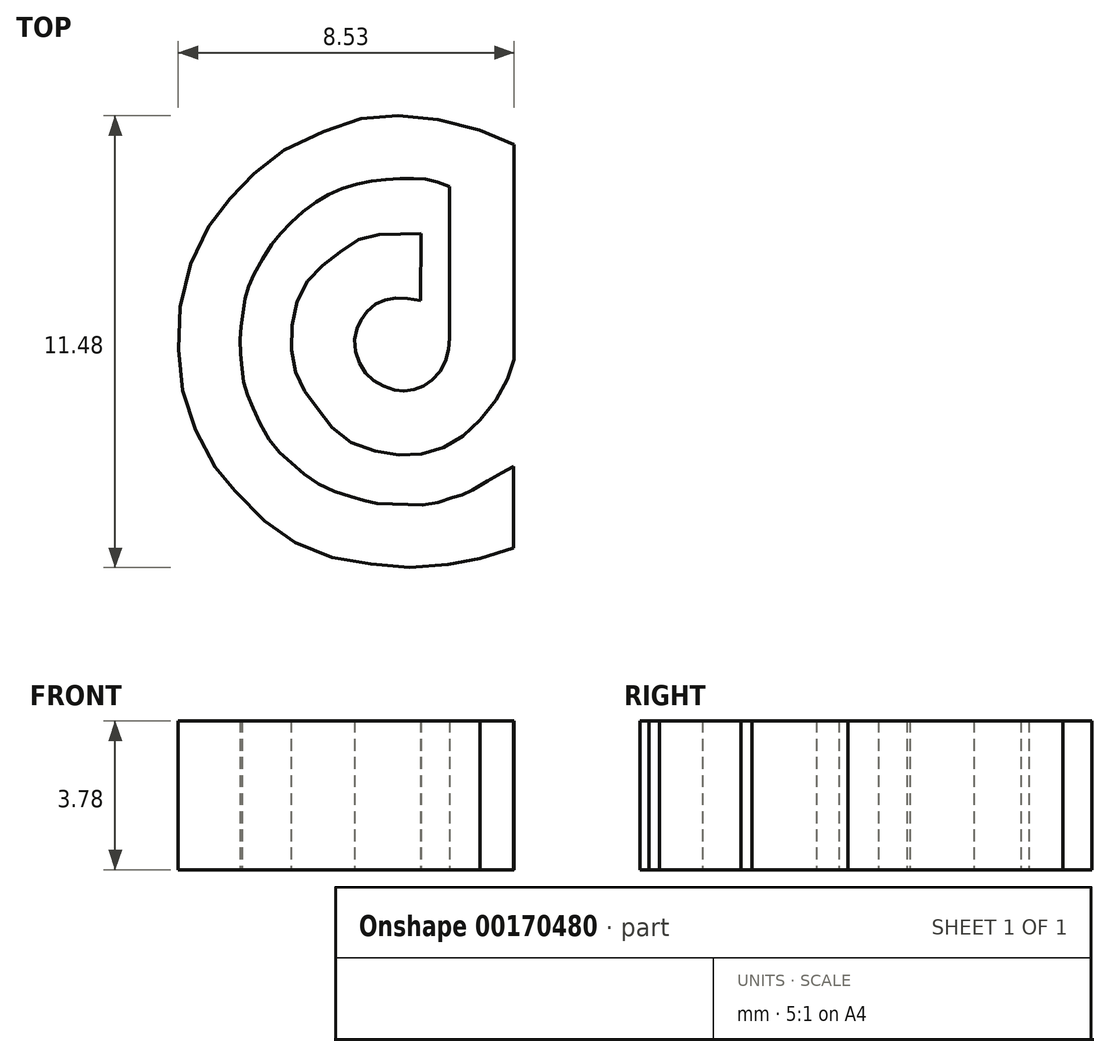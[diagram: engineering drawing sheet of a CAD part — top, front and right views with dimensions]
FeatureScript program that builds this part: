
annotation { "Feature Type Name" : "Feature", "Feature Type Description" : "" }
export const myFeature = defineFeature(function(context is Context, id is Id, definition is map)
    precondition{}
    {
        {
            var Q0;
            Q0=qCreatedBy(makeId("Top.planeOp"),FACE);
            var sketch = newSketch(context, id + "F0", { "sketchPlane" : qUnion([Q0])});
            skFitSpline(sketch, "E0", {"points": [v(23.4, 26.63) * mm, v(22.67, 26.61) * mm, v(21.9, 26.5) * mm, v(21.2, 26.04) * mm, v(20.6, 25.52) * mm, v(20.2, 24.71) * mm, v(20.11, 23.68) * mm, v(20.3, 22.87) * mm, v(20.76, 22.21) * mm, v(21.37, 21.48) * mm, v(22.37, 21.08) * mm, v(23.3, 21) * mm, v(24.15, 21.27) * mm, v(24.85, 21.82) * mm, v(25.5, 22.7) * mm, v(25.77, 23.43) * mm], "startDerivative": vector(-11.94, -0.24) * mm, "endDerivative": vector(3.35, 11.29) * mm});
            skLineSegment(sketch, "E1", {"start": v(25.77, 23.43) * mm, "end": v(25.77, 28.89) * mm});
            skFitSpline(sketch, "E2", {"points": [v(25.77, 28.89) * mm, v(24.88, 29.26) * mm, v(23.67, 29.54) * mm, v(22.63, 29.62) * mm, v(21.68, 29.5) * mm, v(20.6, 29.08) * mm, v(19.53, 28.5) * mm, v(18.93, 27.88) * mm, v(18.33, 27.28) * mm, v(17.85, 26.52) * mm, v(17.37, 25.3) * mm, v(17.24, 24.04) * mm, v(17.31, 22.84) * mm, v(17.63, 21.75) * mm, v(18.18, 20.67) * mm, v(18.57, 20.2) * mm, v(19.4, 19.36) * mm, v(20.16, 18.8) * mm, v(21.17, 18.38) * mm, v(22.2, 18.22) * mm, v(23.22, 18.14) * mm, v(24.21, 18.23) * mm, v(24.9, 18.37) * mm], "startDerivative": vector(-19.04, 9.03) * mm, "endDerivative": vector(17.46, 3.76) * mm});
            skLineSegment(sketch, "E3", {"start": v(25.75, 20.7) * mm, "end": v(25.75, 18.64) * mm});
            skFitSpline(sketch, "E4", {"points": [v(24.9, 18.37) * mm, v(25.75, 18.64) * mm], "startDerivative": vector(0.85, 0.27) * mm, "endDerivative": vector(0.85, 0.27) * mm});
            skFitSpline(sketch, "E5", {"points": [v(25.75, 20.7) * mm, v(25.2, 20.4) * mm, v(24.53, 20.01) * mm, v(24.32, 19.95) * mm, v(23.66, 19.74) * mm, v(23.01, 19.74) * mm, v(22.28, 19.77) * mm, v(21.76, 19.9) * mm, v(20.95, 20.18) * mm, v(20.22, 20.7) * mm, v(19.66, 21.24) * mm, v(19.18, 22.08) * mm, v(18.96, 22.65) * mm, v(18.86, 23.2) * mm], "startDerivative": vector(-6.86, -3.5) * mm, "endDerivative": vector(-0.17, 7.63) * mm});
            skFitSpline(sketch, "E6", {"points": [v(18.86, 23.2) * mm, v(18.8, 23.86) * mm, v(18.86, 24.43) * mm, v(18.96, 25.04) * mm, v(19.14, 25.54) * mm, v(19.59, 26.3) * mm, v(20.01, 26.82) * mm, v(20.65, 27.37) * mm, v(21.23, 27.7) * mm, v(21.95, 27.93) * mm, v(22.6, 28) * mm, v(23.19, 28.02) * mm, v(23.65, 27.99) * mm, v(24.13, 27.82) * mm], "startDerivative": vector(-0.92, 8.73) * mm, "endDerivative": vector(7.09, -2.85) * mm});
            skLineSegment(sketch, "E7", {"start": v(24.13, 27.82) * mm, "end": v(24.13, 24.2) * mm});
            skFitSpline(sketch, "E8", {"points": [v(24.13, 24.2) * mm, v(24.13, 23.93) * mm, v(24.07, 23.5) * mm, v(23.88, 23.12) * mm, v(23.6, 22.83) * mm, v(23.32, 22.7) * mm, v(22.99, 22.62) * mm, v(22.7, 22.66) * mm, v(22.3, 22.82) * mm, v(22, 23.07) * mm, v(21.8, 23.46) * mm, v(21.71, 23.89) * mm, v(21.8, 24.27) * mm, v(21.93, 24.51) * mm, v(22.2, 24.8) * mm, v(22.52, 24.95) * mm, v(22.88, 25) * mm, v(23.39, 24.92) * mm], "startDerivative": vector(0.09, -4.95) * mm, "endDerivative": vector(7.74, -1.48) * mm});
            skLineSegment(sketch, "E9", {"start": v(23.4, 26.63) * mm, "end": v(23.39, 24.92) * mm});
            skSolve(sketch);
        }
        {
            var Q0;
            Q0=makeQuery(id+"F0.imprint","IMPRINT",FACE,{"disambiguationData":[TD([[makeQuery(id+"F0.imprint","IMPRINT",EDGE,{"derivedFrom":sQuery(id+"F0.wireOp",EDGE,"E0")}),1.0]])]});
            extrude(context, id + "F1", {"entities" : qUnion([Q0]), "depth" : 3.78 * mm, "offsetDistance" : 25.4 * mm});
        }
    });
